# Revit family: Control_System-Lutron-X96_Ketra_Controller
name_source: partatom
category: Lighting Fixtures
units: mm (PartAtom-declared; Revit-internal decimal feet)

## family parameters
Cut with Voids When Loaded = Yes
Host = Face
Light Source = No
OmniClass Number = 23.80.30.11.17
OmniClass Title = Distribution Boards and Control Panels
Part Type = Normal
Room Calculation Point = No
Round Connector Dimension = Use Radius
Shared = No

## types (1)
- HW-X96-X-J1
    Apparent Load = 92 VA
    Assembly Code = D5020200
    Cost = 0 $
    Current = 1 A
    Default Elevation = 0' - 0"
    Depth = 0' - 1 5/16"
    Description = The X96 is a beautifully designed Ketra controller used to power and control the Ketra LS0 Lightbar Slim linear. It is a 96W class 2 driver with wireless capability that allows for easy installation in multiple, convenient locations.​ The X96 communicates via the Lutron’s Clear Connect Type X protocol and therefore enables Ketra’s LS0 Lightbar Slim to integrate with Lutron’s commercial and residential control systems, Athena and HomeWorks.
    Finish = Metal - Lutron - BL - Black
    Frequency = 60 Hz
    Height = 0' - 5"
    Instruction Sheet Link = https://www.ketra.com
    Keynote = 26 51 00
    Lamp = -
    Load Classification = Lighting
    Manufacturer = Lutron Electronics Co., Inc
    Manufacturer Fax Number = 610-282-1243
    Model = HW-X96-X-J1
    Number of Poles = 1
    Performance URL = http://www.lutron.com
    Power Factor = 1
    Product Documentation Link = https://www.ketra.com
    Product Name = X96 Ketra Controller
    Product Page URL = https://www.ketra.com
    Series = Ketra
    URL = https://www.ketra.com
    Version = 2019 - v1.0a
    Video Link = https://www.youtube.com
    Voltage = 120 V
    Warranty URL = https://www.ketra.com
    Wattage = 92 W
    Wattage Comments = 92W
    Width = 0' - 5"

## geometry (parser evidence)
native form markers: Sweep x2
no freeform markers — native parametric forms only
